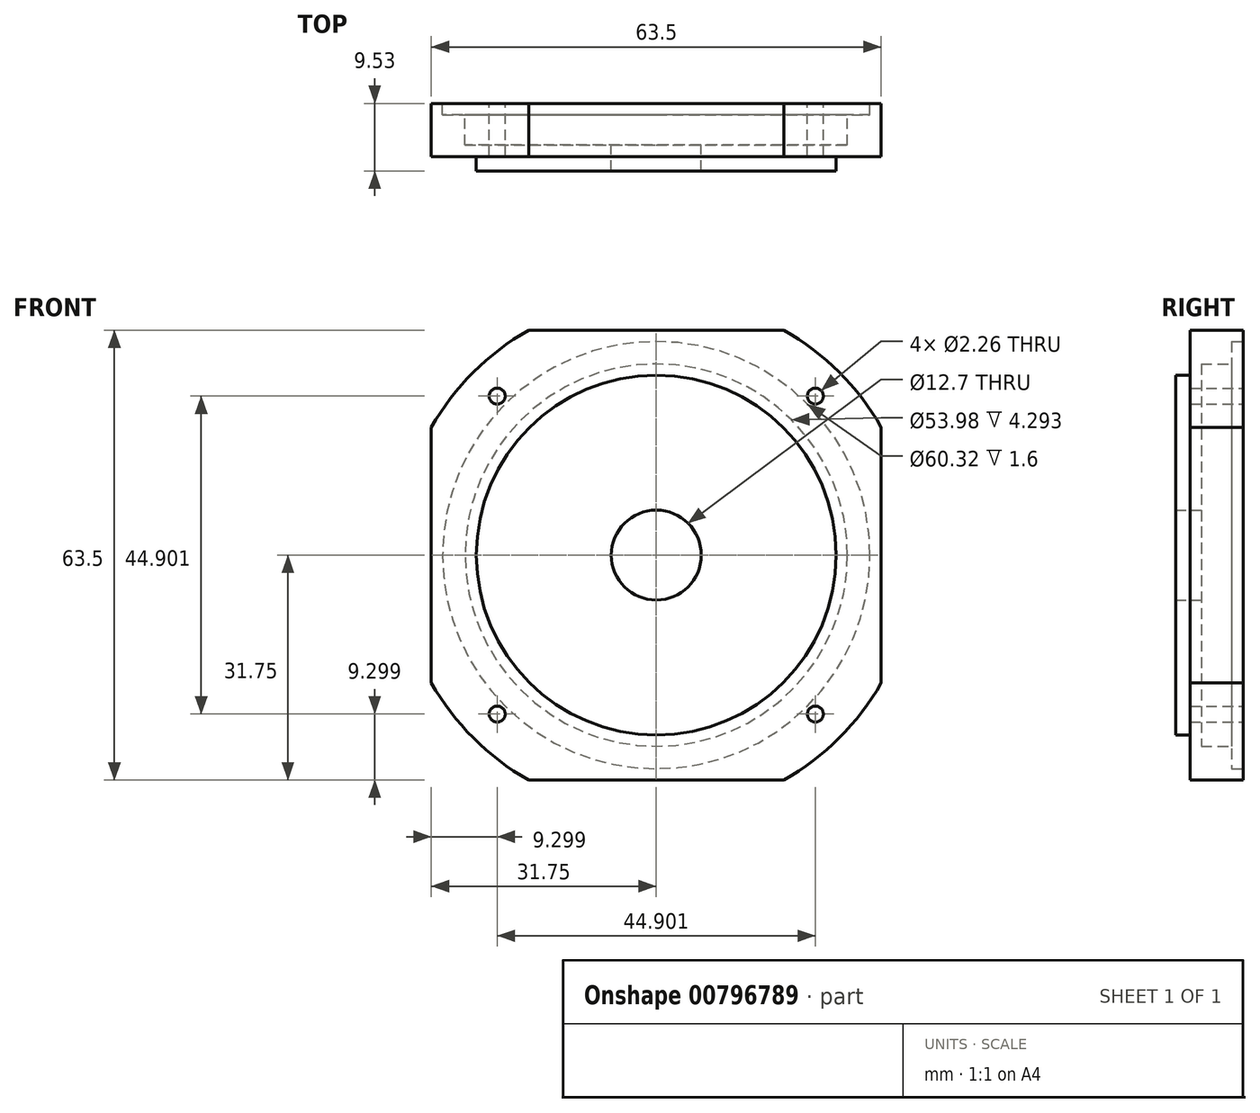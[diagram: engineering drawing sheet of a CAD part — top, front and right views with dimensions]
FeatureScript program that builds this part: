
annotation { "Feature Type Name" : "Feature", "Feature Type Description" : "" }
export const myFeature = defineFeature(function(context is Context, id is Id, definition is map)
    precondition{}
    {
        {
            var Q0;
            Q0=qCreatedBy(makeId("Right.planeOp"),FACE);
            var sketch = newSketch(context, id + "F0", { "sketchPlane" : qUnion([Q0])});
            skLineSegment(sketch, "E0", {"start": v(0, 0) * mm, "end": v(0, 25.4) * mm});
            skLineSegment(sketch, "E1", {"start": v(0, 25.4) * mm, "end": v(2.03, 25.4) * mm});
            skLineSegment(sketch, "E2", {"start": v(2.03, 25.4) * mm, "end": v(2.03, 36.51) * mm});
            skLineSegment(sketch, "E3", {"start": v(2.03, 36.51) * mm, "end": v(9.52, 36.51) * mm});
            skLineSegment(sketch, "E4", {"start": v(9.52, 36.51) * mm, "end": v(9.52, 30.16) * mm});
            skLineSegment(sketch, "E5", {"start": v(9.52, 30.16) * mm, "end": v(7.92, 30.16) * mm});
            skLineSegment(sketch, "E6", {"start": v(7.92, 30.16) * mm, "end": v(7.92, 26.99) * mm});
            skLineSegment(sketch, "E7", {"start": v(7.92, 26.99) * mm, "end": v(3.63, 26.99) * mm});
            skLineSegment(sketch, "E8", {"start": v(3.63, 26.99) * mm, "end": v(3.63, 0) * mm});
            skLineSegment(sketch, "E9", {"start": v(3.63, 0) * mm, "end": v(0, 0) * mm, "construction": true});
            skLineSegment(sketch, "E10", {"start": v(0, 6.35) * mm, "end": v(3.63, 6.35) * mm});
            skSolve(sketch);
        }
        {
            var Q0;
            {var subQ0=sQuery(id+"F0.wireOp",EDGE,"E1");Q0=makeQuery(id+"F0.imprint","IMPRINT",FACE,{"disambiguationData":[TD([[makeQuery(id+"F0.imprint","IMPRINT",EDGE,{"derivedFrom":subQ0}),-1.0]])]});}
            var Q1;
            Q1=sQuery(id+"F0.wireOp",EDGE,"E9");
            revolve(context, id + "F1", {"surfaceOperationType" : NewSurfaceOperationType.NEW, "entities" : qUnion([Q0]), "axis" : qUnion([Q1]), "revolveType" : RevolveType.FULL});
        }
        {
            var Q0;
            Q0=qCreatedBy(makeId("Front.planeOp"),FACE);
            var sketch = newSketch(context, id + "F2", { "sketchPlane" : qUnion([Q0])});
            skLineSegment(sketch, "E11.bottom", {"start": v(31.75, 31.75) * mm, "end": v(-31.75, 31.75) * mm});
            skLineSegment(sketch, "E11.top", {"start": v(31.75, -31.75) * mm, "end": v(-31.75, -31.75) * mm});
            skLineSegment(sketch, "E11.left", {"start": v(31.75, 31.75) * mm, "end": v(31.75, -31.75) * mm});
            skLineSegment(sketch, "E11.right", {"start": v(-31.75, 31.75) * mm, "end": v(-31.75, -31.75) * mm});
            skPoint(sketch, "E11.middle", {"position": v(0, 0) * mm});
            skSolve(sketch);
        }
        {
            var Q0;
            Q0=makeQuery(id+"F2.imprint","IMPRINT",FACE,{"disambiguationData":[TD([[makeQuery(id+"F2.imprint","IMPRINT",EDGE,{"derivedFrom":sQuery(id+"F2.wireOp",EDGE,"E11.bottom")}),1.0]])]});
            extrude(context, id + "F3", {"entities" : qUnion([Q0]), "operationType" : NewBodyOperationType.INTERSECT, "endBound" : BoundingType.THROUGH_ALL, "oppositeDirection" : true, "depth" : 25.4 * mm, "offsetDistance" : 25.4 * mm});
        }
        {
            var Q0;
            Q0=makeQuery(id+"F1.opRevolve","SWEPT_FACE",FACE,{"disambiguationData":[OSD([sQuery(id+"F0.wireOp",EDGE,"E4")])]});
            var sketch = newSketch(context, id + "F4", { "sketchPlane" : qUnion([Q0])});
            skCircle(sketch, "E12", {"center": v(0, 0) * mm, "radius": 31.75 * mm, "construction": true});
            skLineSegment(sketch, "E13", {"start": v(-22.45, 22.45) * mm, "end": v(22.45, -22.45) * mm, "construction": true});
            skLineSegment(sketch, "E14", {"start": v(-22.45, -22.45) * mm, "end": v(22.45, 22.45) * mm, "construction": true});
            skSolve(sketch);
        }
        {
            var Q0;
            Q0=sQuery(id+"F4.wireOp",VERTEX,"E13.start");
            var Q1;
            Q1=sQuery(id+"F4.wireOp",VERTEX,"E14.end");
            var Q2;
            Q2=sQuery(id+"F4.wireOp",VERTEX,"E13.end");
            var Q3;
            Q3=sQuery(id+"F4.wireOp",VERTEX,"E14.start");
            var Q4;
            Q4=makeQuery(id+"F1.opRevolve","SWEPT_BODY",BODY,{"disambiguationData":[OSD([sQuery(id+"F0.wireOp",EDGE,"E0"),sQuery(id+"F0.wireOp",EDGE,"E1"),sQuery(id+"F0.wireOp",EDGE,"E2"),sQuery(id+"F0.wireOp",EDGE,"E3"),sQuery(id+"F0.wireOp",EDGE,"E4"),sQuery(id+"F0.wireOp",EDGE,"E5"),sQuery(id+"F0.wireOp",EDGE,"E6"),sQuery(id+"F0.wireOp",EDGE,"E7"),sQuery(id+"F0.wireOp",EDGE,"E8"),sQuery(id+"F0.wireOp",EDGE,"E10")])]});
            hole(context, id + "F5", {"style" : HoleStyle.SIMPLE, "endStyle" : HoleEndStyle.THROUGH, "standardTappedOrClearance" : lookupTablePath({ "standard" : "ANSI", "engagement" : "75%", "pitch" : "40 tpi", "size" : "#4", "type" : "Tapped" }), "standardBlindInLast" : lookupTablePath({ "standard" : "ANSI", "engagement" : "75%", "pitch" : "40 tpi", "size" : "#4", "type" : "Tapped" }), "holeDiameter" : 2.26 * mm, "majorDiameter" : 2.84 * mm, "showTappedDepth" : true, "isTappedThrough" : true, "tappedDepth" : 12.7 * mm, "tapClearance" : 3, "locations" : qUnion([Q0, Q1, Q2, Q3]), "scope" : qUnion([Q4])});
        }
    });
